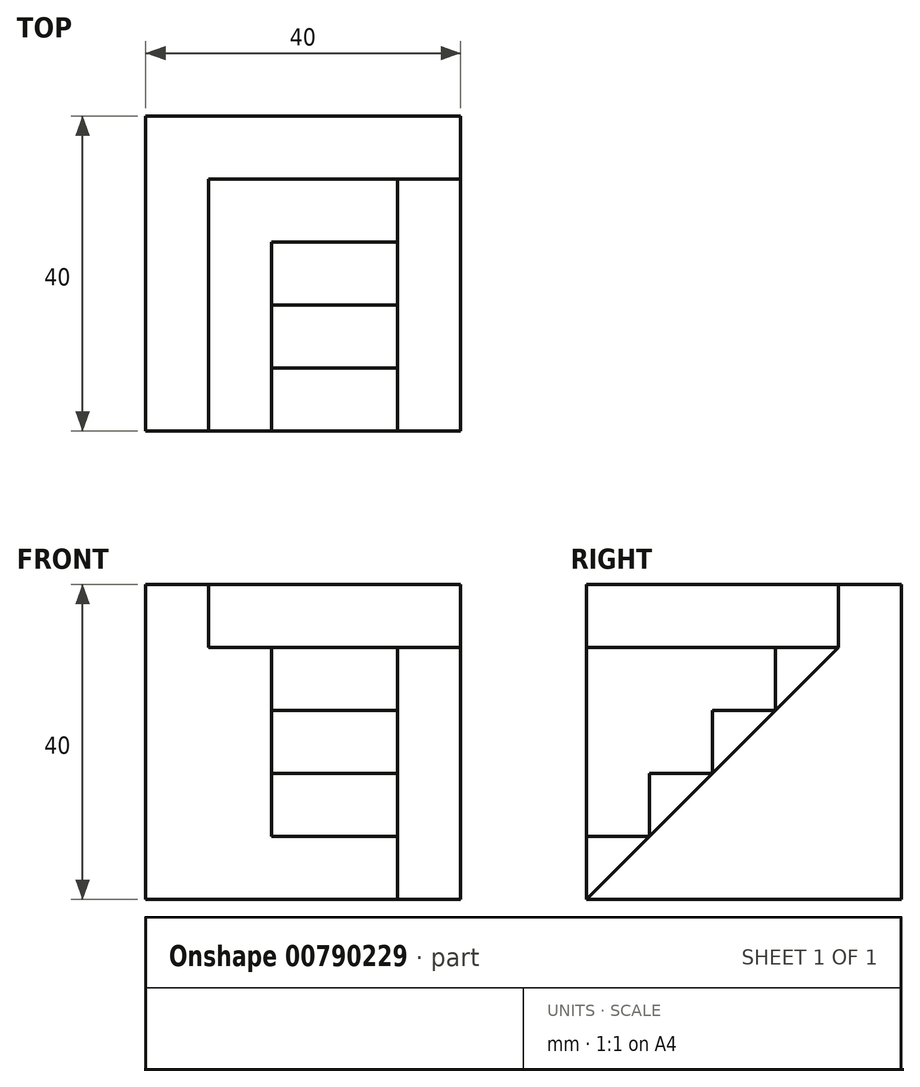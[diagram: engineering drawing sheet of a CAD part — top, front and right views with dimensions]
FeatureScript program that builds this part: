
annotation { "Feature Type Name" : "Feature", "Feature Type Description" : "" }
export const myFeature = defineFeature(function(context is Context, id is Id, definition is map)
    precondition{}
    {
        {
            var Q0;
            Q0=qCreatedBy(makeId("Top.planeOp"),FACE);
            var sketch = newSketch(context, id + "F0", { "sketchPlane" : qUnion([Q0])});
            skLineSegment(sketch, "E0.bottom", {"start": v(20, 20) * mm, "end": v(-20, 20) * mm});
            skLineSegment(sketch, "E0.top", {"start": v(20, -20) * mm, "end": v(-20, -20) * mm});
            skLineSegment(sketch, "E0.left", {"start": v(20, 20) * mm, "end": v(20, -20) * mm});
            skLineSegment(sketch, "E0.right", {"start": v(-20, 20) * mm, "end": v(-20, -20) * mm});
            skPoint(sketch, "E0.middle", {"position": v(0, 0) * mm});
            skLineSegment(sketch, "E1", {"start": v(-12, 12) * mm, "end": v(-12, -20) * mm});
            skLineSegment(sketch, "E2", {"start": v(-12, 12) * mm, "end": v(20, 12) * mm});
            skLineSegment(sketch, "E3", {"start": v(12, 12) * mm, "end": v(12, -20) * mm});
            skLineSegment(sketch, "E4", {"start": v(-4, -20) * mm, "end": v(-4, 4) * mm});
            skLineSegment(sketch, "E5", {"start": v(-4, 4) * mm, "end": v(12, 4) * mm});
            skLineSegment(sketch, "E6", {"start": v(-4, -4) * mm, "end": v(12, -4) * mm});
            skLineSegment(sketch, "E7.trimOffspring", {"start": v(-4, -12) * mm, "end": v(12, -12) * mm});
            skPoint(sketch, "E8.orphan", {"position": v(-4, 12) * mm});
            skPoint(sketch, "E9.start.orphan", {"position": v(-20, -12) * mm});
            skSolve(sketch);
        }
        {
            var Q0;
            {var subQ1=sQuery(id+"F0.wireOp",EDGE,"E0.left");var subQ6=sQuery(id+"F0.wireOp",EDGE,"E0.top");var subQ7=makeQuery(id+"F0.imprint","INTERSECT",VERTEX,{"derivedFrom":[subQ6,subQ1]});Q0=makeQuery(id+"F0.imprint","IMPRINT",FACE,{"disambiguationData":[TD([[makeQuery(id+"F0.imprint","IMPRINT",EDGE,{"disambiguationData":[TD([[subQ7,-1.0]])],"derivedFrom":subQ6}),-1.0]])]});}
            extrude(context, id + "F1", {"entities" : qUnion([Q0]), "depth" : 32 * mm, "offsetDistance" : 25 * mm});
        }
        {
            var Q0;
            Q0=makeQuery(id+"F1.opExtrude","SWEPT_FACE",FACE,{"disambiguationData":[OSD([sQuery(id+"F0.wireOp",EDGE,"E0.left")])]});
            var sketch = newSketch(context, id + "F2", { "sketchPlane" : qUnion([Q0])});
            skLineSegment(sketch, "E10", {"start": v(-20, 0) * mm, "end": v(12, 32) * mm});
            skSolve(sketch);
        }
        {
            var Q0;
            Q0=makeQuery(id+"F2.imprint","IMPRINT",FACE,{"disambiguationData":[TD([[makeQuery(id+"F2.imprint","IMPRINT",EDGE,{"derivedFrom":sQuery(id+"F2.wireOp",EDGE,"E10")}),1.0]])]});
            extrude(context, id + "F3", {"entities" : qUnion([Q0]), "operationType" : NewBodyOperationType.REMOVE, "oppositeDirection" : true, "depth" : 25 * mm, "offsetDistance" : 25 * mm});
        }
        {
            var Q0;
            {var subQ4=sQuery(id+"F0.wireOp",EDGE,"E0.bottom");Q0=makeQuery(id+"F0.imprint","IMPRINT",FACE,{"disambiguationData":[TD([[makeQuery(id+"F0.imprint","IMPRINT",EDGE,{"derivedFrom":subQ4}),1.0]])]});}
            extrude(context, id + "F4", {"entities" : qUnion([Q0]), "operationType" : NewBodyOperationType.ADD, "depth" : 40 * mm, "offsetDistance" : 25 * mm});
        }
        {
            var Q0;
            {var subQ4=sQuery(id+"F0.wireOp",EDGE,"E1");Q0=makeQuery(id+"F0.imprint","IMPRINT",FACE,{"disambiguationData":[TD([[makeQuery(id+"F0.imprint","IMPRINT",EDGE,{"derivedFrom":subQ4}),1.0]])]});}
            extrude(context, id + "F5", {"entities" : qUnion([Q0]), "operationType" : NewBodyOperationType.ADD, "depth" : 32 * mm, "offsetDistance" : 25 * mm});
        }
        {
            var Q0;
            {var subQ0=sQuery(id+"F0.wireOp",EDGE,"E5");Q0=makeQuery(id+"F0.imprint","IMPRINT",FACE,{"disambiguationData":[TD([[makeQuery(id+"F0.imprint","IMPRINT",EDGE,{"derivedFrom":subQ0}),-1.0]])]});}
            extrude(context, id + "F6", {"entities" : qUnion([Q0]), "operationType" : NewBodyOperationType.ADD, "depth" : 24 * mm, "offsetDistance" : 25 * mm});
        }
        {
            var Q0;
            {var subQ0=sQuery(id+"F0.wireOp",EDGE,"E6");Q0=makeQuery(id+"F0.imprint","IMPRINT",FACE,{"disambiguationData":[TD([[makeQuery(id+"F0.imprint","IMPRINT",EDGE,{"derivedFrom":subQ0}),-1.0]])]});}
            extrude(context, id + "F7", {"entities" : qUnion([Q0]), "operationType" : NewBodyOperationType.ADD, "depth" : 16 * mm, "offsetDistance" : 25 * mm});
        }
        {
            var Q0;
            {var subQ5=sQuery(id+"F0.wireOp",EDGE,"E7.trimOffspring");Q0=makeQuery(id+"F0.imprint","IMPRINT",FACE,{"disambiguationData":[TD([[makeQuery(id+"F0.imprint","IMPRINT",EDGE,{"derivedFrom":subQ5}),-1.0]])]});}
            extrude(context, id + "F8", {"entities" : qUnion([Q0]), "operationType" : NewBodyOperationType.ADD, "depth" : 8 * mm, "offsetDistance" : 25 * mm});
        }
    });
